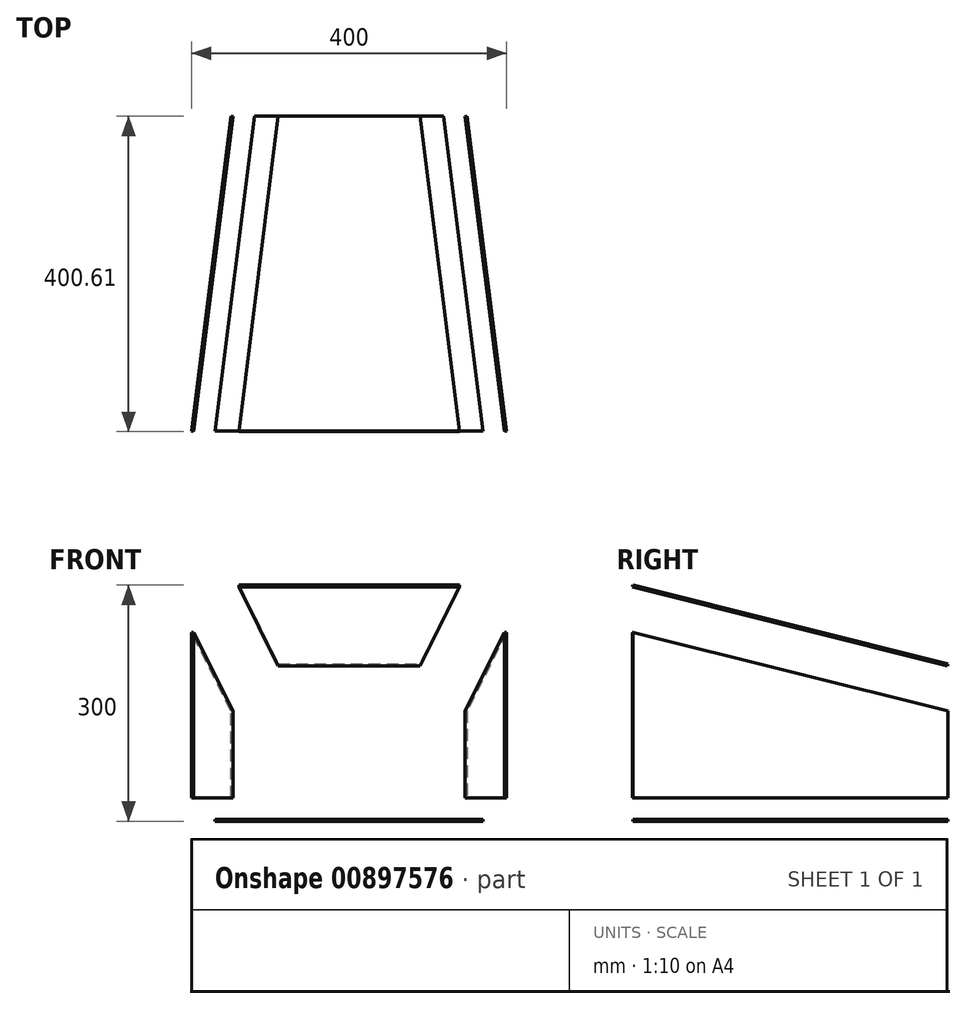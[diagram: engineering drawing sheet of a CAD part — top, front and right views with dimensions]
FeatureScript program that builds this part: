
annotation { "Feature Type Name" : "Feature", "Feature Type Description" : "" }
export const myFeature = defineFeature(function(context is Context, id is Id, definition is map)
    precondition{}
    {
        {
            var Q0;
            Q0=qCreatedBy(makeId("Front.planeOp"),FACE);
            var sketch = newSketch(context, id + "F0", { "sketchPlane" : qUnion([Q0])});
            skLineSegment(sketch, "E0.bottom", {"start": v(170, -150) * mm, "end": v(-170, -150) * mm});
            skLineSegment(sketch, "E0.top", {"start": v(140, 150) * mm, "end": v(-140, 150) * mm});
            skLineSegment(sketch, "E0.left", {"start": v(200, -120) * mm, "end": v(200, 90) * mm});
            skLineSegment(sketch, "E0.right", {"start": v(-200, -120) * mm, "end": v(-200, 90) * mm});
            skPoint(sketch, "E0.middle", {"position": v(0, 0) * mm});
            skLineSegment(sketch, "E1.bottom", {"start": v(168, -148) * mm, "end": v(-168, -148) * mm});
            skLineSegment(sketch, "E1.top", {"start": v(138, 148) * mm, "end": v(-138, 148) * mm});
            skLineSegment(sketch, "E1.left", {"start": v(198, -118) * mm, "end": v(198, 88) * mm});
            skLineSegment(sketch, "E1.right", {"start": v(-198, -118) * mm, "end": v(-198, 88) * mm});
            skPoint(sketch, "E2.visualSharp", {"position": v(198, 148) * mm});
            skArc(sketch, "E2.filletArc", {"start": v(198, 88) * mm, "mid": v(180.43, 130.43) * mm, "end": v(138, 148) * mm});
            skPoint(sketch, "E3.visualSharp", {"position": v(200, 150) * mm});
            skArc(sketch, "E3.filletArc", {"start": v(200, 90) * mm, "mid": v(182.43, 132.43) * mm, "end": v(140, 150) * mm});
            skPoint(sketch, "E4.visualSharp", {"position": v(-198, 148) * mm});
            skArc(sketch, "E4.filletArc", {"start": v(-138, 148) * mm, "mid": v(-180.43, 130.43) * mm, "end": v(-198, 88) * mm});
            skPoint(sketch, "E5.visualSharp", {"position": v(-200, 150) * mm});
            skArc(sketch, "E5.filletArc", {"start": v(-140, 150) * mm, "mid": v(-182.43, 132.43) * mm, "end": v(-200, 90) * mm});
            skPoint(sketch, "E6.visualSharp", {"position": v(198, -148) * mm});
            skArc(sketch, "E6.filletArc", {"start": v(168, -148) * mm, "mid": v(189.21, -139.21) * mm, "end": v(198, -118) * mm});
            skPoint(sketch, "E7.visualSharp", {"position": v(200, -150) * mm});
            skArc(sketch, "E7.filletArc", {"start": v(170, -150) * mm, "mid": v(191.21, -141.21) * mm, "end": v(200, -120) * mm});
            skPoint(sketch, "E8.visualSharp", {"position": v(-198, -148) * mm});
            skArc(sketch, "E8.filletArc", {"start": v(-198, -118) * mm, "mid": v(-189.21, -139.21) * mm, "end": v(-168, -148) * mm});
            skPoint(sketch, "E9.visualSharp", {"position": v(-200, -150) * mm});
            skArc(sketch, "E9.filletArc", {"start": v(-200, -120) * mm, "mid": v(-191.21, -141.21) * mm, "end": v(-170, -150) * mm});
            skSolve(sketch);
        }
        {
            var Q0;
            Q0=qCreatedBy(makeId("Front.planeOp"),FACE);
            cPlane(context, id + "F1", {"entities" : qUnion([Q0]), "cplaneType" : CPlaneType.OFFSET, "offset" : 400 * mm, "oppositeDirection" : true, "width" : 150 * mm, "height" : 150 * mm});
        }
        {
            var Q0;
            Q0=qCreatedBy(id+"F1.planeOp",FACE);
            var sketch = newSketch(context, id + "F2", { "sketchPlane" : qUnion([Q0])});
            skLineSegment(sketch, "E10.bottom", {"start": v(-120, -150) * mm, "end": v(120, -150) * mm});
            skLineSegment(sketch, "E10.top", {"start": v(-90, 50) * mm, "end": v(90, 50) * mm});
            skLineSegment(sketch, "E10.left", {"start": v(-150, -120) * mm, "end": v(-150, -10) * mm});
            skLineSegment(sketch, "E10.right", {"start": v(150, -120) * mm, "end": v(150, -10) * mm});
            skPoint(sketch, "E10.middle", {"position": v(0, -50) * mm});
            skLineSegment(sketch, "E11.bottom", {"start": v(-118, -148) * mm, "end": v(118, -148) * mm});
            skLineSegment(sketch, "E11.top", {"start": v(-88, 48) * mm, "end": v(88, 48) * mm});
            skLineSegment(sketch, "E11.left", {"start": v(-148, -118) * mm, "end": v(-148, -12) * mm});
            skLineSegment(sketch, "E11.right", {"start": v(148, -118) * mm, "end": v(148, -12) * mm});
            skPoint(sketch, "E12.visualSharp", {"position": v(148, 48) * mm});
            skArc(sketch, "E12.filletArc", {"start": v(148, -12) * mm, "mid": v(130.43, 30.43) * mm, "end": v(88, 48) * mm});
            skPoint(sketch, "E13.visualSharp", {"position": v(-148, 48) * mm});
            skArc(sketch, "E13.filletArc", {"start": v(-88, 48) * mm, "mid": v(-130.43, 30.43) * mm, "end": v(-148, -12) * mm});
            skPoint(sketch, "E14.visualSharp", {"position": v(-150, 50) * mm});
            skArc(sketch, "E14.filletArc", {"start": v(-90, 50) * mm, "mid": v(-132.43, 32.43) * mm, "end": v(-150, -10) * mm});
            skPoint(sketch, "E15.visualSharp", {"position": v(150, 50) * mm});
            skArc(sketch, "E15.filletArc", {"start": v(150, -10) * mm, "mid": v(132.43, 32.43) * mm, "end": v(90, 50) * mm});
            skPoint(sketch, "E16.visualSharp", {"position": v(148, -148) * mm});
            skArc(sketch, "E16.filletArc", {"start": v(118, -148) * mm, "mid": v(139.21, -139.21) * mm, "end": v(148, -118) * mm});
            skPoint(sketch, "E17.visualSharp", {"position": v(150, -150) * mm});
            skArc(sketch, "E17.filletArc", {"start": v(120, -150) * mm, "mid": v(141.21, -141.21) * mm, "end": v(150, -120) * mm});
            skPoint(sketch, "E18.visualSharp", {"position": v(-148, -148) * mm});
            skArc(sketch, "E18.filletArc", {"start": v(-148, -118) * mm, "mid": v(-139.21, -139.21) * mm, "end": v(-118, -148) * mm});
            skPoint(sketch, "E19.visualSharp", {"position": v(-150, -150) * mm});
            skArc(sketch, "E19.filletArc", {"start": v(-150, -120) * mm, "mid": v(-141.21, -141.21) * mm, "end": v(-120, -150) * mm});
            skSolve(sketch);
        }
        {
            var Q0;
            Q0=sQuery(id+"F0.wireOp",EDGE,"E0.top");
            var Q1;
            Q1=sQuery(id+"F2.wireOp",EDGE,"E10.top");
            cPlane(context, id + "F3", {"entities" : qUnion([Q0, Q1]), "cplaneType" : CPlaneType.LINE_ANGLE, "offset" : 25 * mm, "angle" : 0 * degree, "width" : 150 * mm, "height" : 150 * mm});
        }
        {
            var Q0;
            Q0=qCreatedBy(id+"F3.planeOp",FACE);
            var sketch = newSketch(context, id + "F4", { "sketchPlane" : qUnion([Q0])});
            skLineSegment(sketch, "E20", {"start": v(140, 36.38) * mm, "end": v(90, -375.93) * mm});
            skLineSegment(sketch, "E21", {"start": v(140, 36.38) * mm, "end": v(-140, 36.38) * mm});
            skLineSegment(sketch, "E22", {"start": v(-140, 36.38) * mm, "end": v(-90, -375.93) * mm});
            skLineSegment(sketch, "E23", {"start": v(-90, -375.93) * mm, "end": v(90, -375.93) * mm});
            skSolve(sketch);
        }
        {
            var Q0;
            Q0 = qSketchRegion(id + "F4", true);
            extrude(context, id + "F5", {"entities" : qUnion([Q0]), "depth" : 2.5 * mm, "offsetDistance" : 25 * mm});
        }
        {
            var Q0;
            Q0=sQuery(id+"F0.wireOp",EDGE,"E0.left");
            var Q1;
            Q1=sQuery(id+"F2.wireOp",EDGE,"E10.right");
            cPlane(context, id + "F6", {"entities" : qUnion([Q0, Q1]), "cplaneType" : CPlaneType.LINE_ANGLE, "offset" : 25 * mm, "angle" : 0 * degree, "width" : 150 * mm, "height" : 150 * mm});
        }
        {
            var Q0;
            Q0=qCreatedBy(id+"F6.planeOp",FACE);
            var sketch = newSketch(context, id + "F7", { "sketchPlane" : qUnion([Q0])});
            skLineSegment(sketch, "E24", {"start": v(24.8, 90) * mm, "end": v(-378.3, -10) * mm});
            skLineSegment(sketch, "E25", {"start": v(-378.3, -10) * mm, "end": v(-378.3, -120) * mm});
            skLineSegment(sketch, "E26", {"start": v(-378.3, -120) * mm, "end": v(24.8, -120) * mm});
            skLineSegment(sketch, "E27", {"start": v(24.8, -120) * mm, "end": v(24.8, 90) * mm});
            skSolve(sketch);
        }
        {
            var Q0;
            Q0 = qSketchRegion(id + "F7", true);
            extrude(context, id + "F8", {"entities" : qUnion([Q0]), "depth" : 2.5 * mm, "offsetDistance" : 25 * mm});
        }
        {
            var Q0;
            Q0=sQuery(id+"F2.wireOp",EDGE,"E10.left");
            var Q1;
            Q1=sQuery(id+"F0.wireOp",EDGE,"E0.right");
            cPlane(context, id + "F9", {"entities" : qUnion([Q0, Q1]), "cplaneType" : CPlaneType.LINE_ANGLE, "offset" : 25 * mm, "angle" : 0 * degree, "width" : 150 * mm, "height" : 150 * mm});
        }
        {
            var Q0;
            Q0=qCreatedBy(id+"F9.planeOp",FACE);
            var sketch = newSketch(context, id + "F10", { "sketchPlane" : qUnion([Q0])});
            skLineSegment(sketch, "E28", {"start": v(378.3, -10) * mm, "end": v(-24.8, 90) * mm});
            skLineSegment(sketch, "E29", {"start": v(-24.8, 90) * mm, "end": v(-24.8, -120) * mm});
            skLineSegment(sketch, "E30", {"start": v(-24.8, -120) * mm, "end": v(378.3, -120) * mm});
            skLineSegment(sketch, "E31", {"start": v(378.3, -120) * mm, "end": v(378.3, -10) * mm});
            skSolve(sketch);
        }
        {
            var Q0;
            Q0 = qSketchRegion(id + "F10", true);
            extrude(context, id + "F11", {"entities" : qUnion([Q0]), "depth" : 2.5 * mm, "offsetDistance" : 25 * mm});
        }
        {
            var Q0;
            Q0=sQuery(id+"F2.wireOp",EDGE,"E10.bottom");
            var Q1;
            Q1=sQuery(id+"F0.wireOp",EDGE,"E0.bottom");
            cPlane(context, id + "F12", {"entities" : qUnion([Q0, Q1]), "cplaneType" : CPlaneType.LINE_ANGLE, "offset" : 25 * mm, "angle" : 0 * degree, "width" : 150 * mm, "height" : 150 * mm});
        }
        {
            var Q0;
            Q0=qCreatedBy(id+"F12.planeOp",FACE);
            var sketch = newSketch(context, id + "F13", { "sketchPlane" : qUnion([Q0])});
            skLineSegment(sketch, "E32", {"start": v(-120, -400) * mm, "end": v(-170, 0) * mm});
            skLineSegment(sketch, "E33", {"start": v(-170, 0) * mm, "end": v(170, 0) * mm});
            skLineSegment(sketch, "E34", {"start": v(170, 0) * mm, "end": v(120, -400) * mm});
            skLineSegment(sketch, "E35", {"start": v(120, -400) * mm, "end": v(-120, -400) * mm});
            skSolve(sketch);
        }
        {
            var Q0;
            Q0 = qSketchRegion(id + "F13", true);
            extrude(context, id + "F14", {"entities" : qUnion([Q0]), "oppositeDirection" : true, "depth" : 2.5 * mm, "offsetDistance" : 25 * mm});
        }
    });
